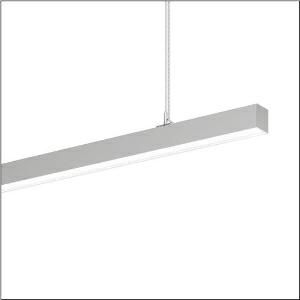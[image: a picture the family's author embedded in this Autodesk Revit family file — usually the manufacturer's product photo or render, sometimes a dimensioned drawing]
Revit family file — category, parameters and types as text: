
# Revit family: silica_r__21_51mx33dc3dsb_c168
name_source: partatom
category: Lighting Fixtures
units: mm (PartAtom-declared; Revit-internal decimal feet)

## family parameters
Cut with Voids When Loaded = No
Host = Face
Light Source = No
Part Type = Normal
Room Calculation Point = No
Round Connector Dimension = Use Diameter
Shared = No

## types (1)
- --- (1 x LED, 14780 lm, 99.5 W, 3000K)
    Apparent Load = 100 VA
    CIE Flux Codes = 78 96 99 55 100
    Color Rendering = 80
    Color Temperature = 3000K
    Default Elevation = 1800 mm
    Description = Silica® 21, office luminaire, primary optical cover: prismatic diffuser, of PMMA, CAT 2 (L<= 3000cd/m²), light emission: direct/indirect distribution, primary light characteristic: symmetric, installation type: suspended mounting, LED, rated luminous flux: 14.780lm, luminous efficacy: 149lm/W, light colour: 830, colour temperature: 3000K, with terminal, 3+2-pole, max. 2.5mm², mains connection: 220..240V, AC, 50/60Hz, rated input power: 99.5W, luminaire housing, of aluminium, metallic grey (RAL 9006), length: 3.004mm, width: 53mm, height: 53mm, protection rating (complete): IP20, insulation class (complete): insulation class I (protective earthing), certification: CE, permissible operating ambient temperature: 0..+35°C, standard: EN 50419, packaging unit: 1 piece
    Height = 53 mm
    Lamp = 1 x LED
    Lamp Light Flux = 14780 lm
    Lamp Power = 99.5 W
    Lamp count = 1
    Length = 3004 mm
    Luminous efficacy = 149 lm/W
    Manufacturer = Siteco
    ModVariant = No
    Model = 51MX33DC3DSB
    Mounting Place = Ceiling
    Mounting Type = Pendant
    Number of Poles = 1
    OnlyDefault = Yes
    Power Factor = 1
    Product Name = Silica® 21
    Product group = office luminaire | ceiling pendant
    ProductGroupID = 902
    Protection Class = Protection class I
    Protection Degree = IP 20
    RLX_Detail_Level = 1
    RLX_Emergency_Light_Flux = 0 lm
    RLX_Emergency_Type = 0
    RLX_Emergency_Type_DB = No
    RlxData = <blob elided: 23485 chars, md5=d4b6f4ce>
    Socket = socket
    Standby Power = 0 W
    System Light Flux = 14780 lm
    System Power = 100 W
    Type Comments = factory setting: luminous flux: 100 % | dim-lin: 254 | 345 mA
    Type Image = l_1297747.jpg
    URL = http://relux.com
    VarID = @adj_048821
    Voltage = 0 V
    Weight = 0.00 kg
    Width = 53 mm

## geometry (parser evidence)
native form markers: Blend x4, Sweep x13
no freeform markers — native parametric forms only
